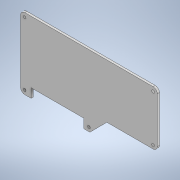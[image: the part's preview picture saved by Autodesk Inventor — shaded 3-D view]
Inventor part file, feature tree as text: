
AUTODESK INVENTOR PART (.ipt)
format: ipt  version: 2021 (Build 250183000, 183)  size: 140,288 bytes
history: native  units: mm
features: sketch x3, extrude x2, hole x1, fillet x1
ambient origin geometry x8: Origin, YZ Plane, XZ Plane, XY Plane, X Axis, Y Axis, Z Axis, Center Point
bodies: Solid1 (feature_tree)
feature tree (7):
  extrude  "Extrusion1"  Depth=52.0mm
  hole  "Hole1"  [1 undecoded]
  extrude  "Extrusion2"  Depth=3.0mm
  fillet  "Fillet1"  Radius=3.0mm
  sketch  "Sketch1"  dims[d0=100.0mm d1=52.0mm]
  sketch  "Sketch2"  dims[d2=50.0mm d3=26.0mm]
  sketch  "Sketch3"  dims[d4=1.6mm d5=0.0mm d6=3.0mm d7=3.0mm d8=50.0mm d9=3.0mm d10=97.0mm d11=15.0mm d12=3.0mm d13=49.0mm d14=97.0mm d15=49.0mm d16=2.0mm d17=6.0mm d18=4.0mm d19=2.0mm d20=90.0deg d21=10.0mm d22=20.594885mm d23=7.7mm d24=6.7mm d25=46.4mm d26=50.7mm d27=63.1mm d28=12.5mm d29=1.6mm d30=0.0mm d31=3.0mm]
note: 1 required parameter value undecoded (feature->parameter linkage not recoverable at this tier; creation-order binding heuristic only, values carry confidence <= 0.55)
